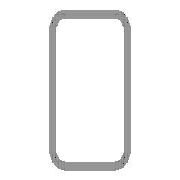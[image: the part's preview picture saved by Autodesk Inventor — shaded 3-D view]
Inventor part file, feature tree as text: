
AUTODESK INVENTOR PART (.ipt)
format: ipt  version: 2025.1 (Build 291241020, 241B)  size: 134,656 bytes
history: native  units: mm (DEFAULTED — no unit token found)
features: other x4, sketch x1, plane x1
ambient origin geometry x8: Origin, YZ Plane, XZ Plane, XY Plane, X Axis, Y Axis, Z Axis, Center Point
bodies: Solid1 (feature_tree), Body (feature_tree)
feature tree (6):
  parser-record x1  (decoder bookkeeping rows leaked as tree rows — omitted from the tree; the rows remain in map.json)
  other  "Driven Length"
  other  "Start Plane"
  other  "End Plane"
  sketch  "Sketch3"  dims[d3=200.0mm d4=0.0mm d7=4.0mm d9=20.0mm d11=40.0mm d12=2.0mm d13=20.0mm d14=220.0mm d15=10.0mm d16=20.0mm d17=90.0deg d18=200.0mm]
  plane  "Work Plane3"
